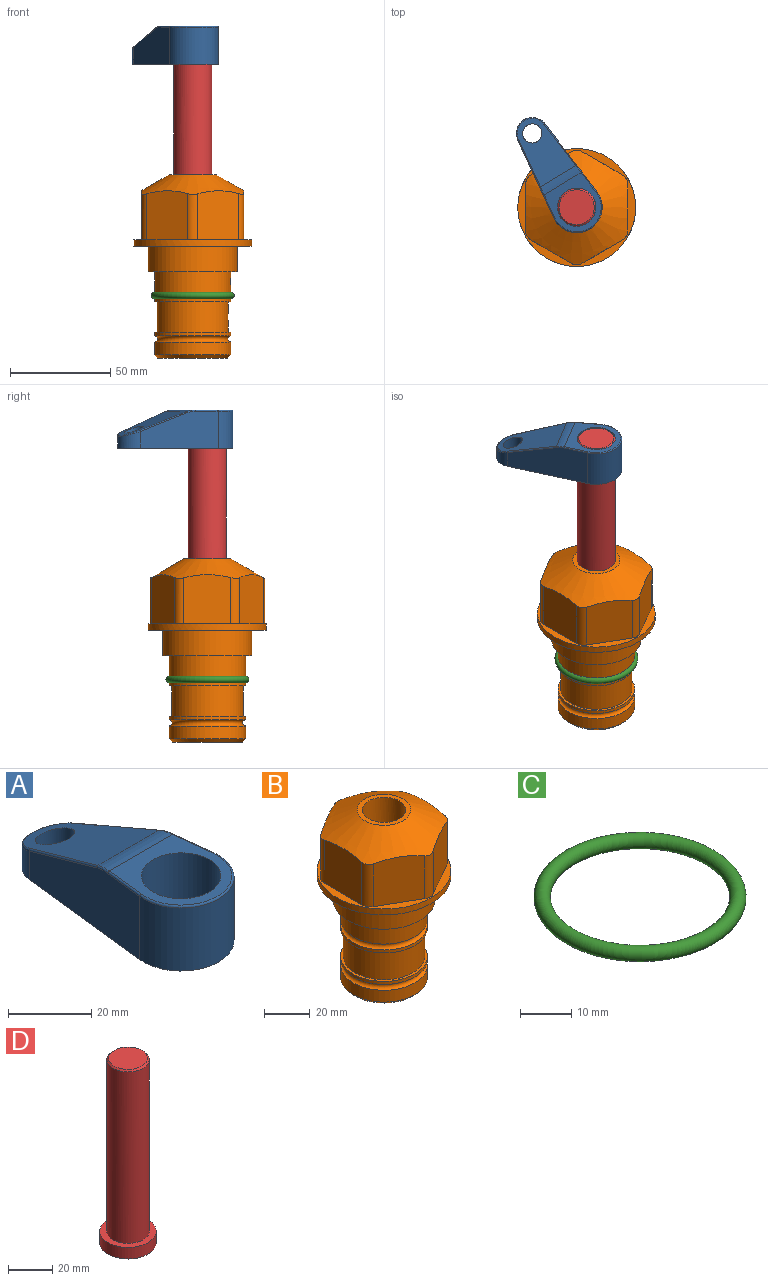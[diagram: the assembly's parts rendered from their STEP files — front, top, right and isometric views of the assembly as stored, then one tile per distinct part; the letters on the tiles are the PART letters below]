
ASSEMBLY  parts=4 mates=2
PART A: 44 faces, bbox 27.5x64.5x19.1 mm
  f0: plane 2.3x0.95mm, normal (0,0,-1), area 1mm2, adj f25,f30,f34
  f1: plane 63.5x25.4mm, normal (0,0,-1), area 561.7mm2, adj f2,f3,f4,f5,f6,f7,f19,f20
  f2: cylinder r=12.7mm len=25.4mm, axis (0,0,-1), area 792.2mm2, adj f1,f3,f5,f13
  f3: plane 42.33x18.54mm, normal (0.99,0.11,0), area 647mm2, adj f1,f2,f4,f11,f12,f14
  f4: cylinder r=7.94mm len=15.78mm, axis (0,0,-1), area 158.6mm2, adj f1,f3,f5,f16
  f5: plane 42.33x18.54mm, normal (-0.99,0.11,0), area 647mm2, adj f1,f2,f4,f15,f17,f18
  f6: cylinder r=9.53mm len=19.05mm, axis (0,0,-1), area 1140.1mm2, adj f1,f8
  f7: cylinder r=4.76mm len=10.98mm, axis (0,0,-1), area 276.1mm2, adj f1,f9
  f8: plane 25.83x24.38mm, normal (0,0,1), area 262.2mm2, adj f6,f10,f11,f13,f15
  f9: plane 32.49x20.55mm, normal (0,0.34,0.94), area 489.9mm2, adj f7,f10,f14,f16,f18
  f10: cylinder r=12.7mm len=21.49mm, axis (-1,0,0), area 93.2mm2, adj f8,f9,f12,f17
  f11: cylinder r=0.51mm len=12.34mm, axis (0.11,-0.99,0), area 9.9mm2, adj f3,f8,f12,f13
  f12: bspline ~7.62x1.64mm, area 3.5mm2, adj f3,f10,f11,f14
  f13: torus R=12.19mm, axis (0,0,1), area 33.6mm2, adj f2,f8,f11,f15
  f14: cylinder r=0.51mm len=26.01mm, axis (0.1,-0.93,0.34), area 21.6mm2, adj f3,f9,f12,f16
  f15: cylinder r=0.51mm len=12.34mm, axis (0.11,0.99,0), area 9.9mm2, adj f5,f8,f13,f17
  f16: bspline ~15.78x7.05mm, area 15.7mm2, adj f4,f9,f14,f18
  f17: bspline ~7.62x1.64mm, area 3.5mm2, adj f5,f10,f15,f18
  f18: cylinder r=0.51mm len=26.01mm, axis (0.1,0.93,-0.34), area 21.6mm2, adj f5,f9,f16,f17
  f19: plane 21.6x14.29mm, normal (-0.99,-0.11,0), area 242.6mm2, adj f1,f26,f28,f34,f36,f38
  f20: plane 21.6x14.29mm, normal (0.99,-0.11,0), area 242.6mm2, adj f1,f27,f29,f37,f39,f41
  f21: cylinder r=12.7mm len=14.29mm, axis (0,0,-1), area 173.2mm2, adj f1,f26,f27,f30,f31,f33
  f22: cylinder r=7.94mm len=7.63mm, axis (0,0,-1), area 53.8mm2, adj f1,f28,f29,f42
  f23: plane 2.3x0.95mm, normal (0,0,-1), area 1mm2, adj f25,f33,f37
  f24: plane 17.94x12.32mm, normal (0,-0.34,-0.94), area 191.2mm2, adj f25,f38,f41,f42
  f25: cylinder r=9.53mm len=12.93mm, axis (-1,0,0), area 37.5mm2, adj f0,f23,f24,f31,f36,f39
  f26: cylinder r=1.59mm len=14.29mm, axis (0,0,-1), area 49mm2, adj f1,f19,f21,f32
  f27: cylinder r=1.59mm len=14.29mm, axis (0,0,-1), area 49mm2, adj f1,f20,f21,f35
  f28: cylinder r=1.59mm len=7.28mm, axis (0,0,-1), area 22.1mm2, adj f1,f19,f22,f40
  f29: cylinder r=1.59mm len=7.28mm, axis (0,0,-1), area 22.1mm2, adj f1,f20,f22,f43
  f30: torus R=14.29mm, axis (0,0,1), area 5.8mm2, adj f0,f21,f31,f32
  f31: bspline ~11.06x2.73mm, area 20.8mm2, adj f21,f25,f30,f33
  f32: sphere r=1.59mm, area 5.4mm2, adj f26,f30,f34
  f33: torus R=14.29mm, axis (0,0,1), area 5.8mm2, adj f21,f23,f31,f35
  f34: cylinder r=1.59mm len=1.68mm, axis (-0.11,0.99,0), area 2.4mm2, adj f0,f19,f32,f36
  f35: sphere r=1.59mm, area 5.4mm2, adj f27,f33,f37
  f36: bspline ~5.82x2.33mm, area 7.7mm2, adj f19,f25,f34,f38
  f37: cylinder r=1.59mm len=1.68mm, axis (0.11,0.99,0), area 2.4mm2, adj f20,f23,f35,f39
  f38: cylinder r=1.59mm len=18.33mm, axis (0.1,-0.93,0.34), area 46.7mm2, adj f19,f24,f36,f40
  f39: bspline ~5.82x2.33mm, area 7.7mm2, adj f20,f25,f37,f41
  f40: sphere r=1.59mm, area 3.6mm2, adj f28,f38,f42
  f41: cylinder r=1.59mm len=18.33mm, axis (0.1,0.93,-0.34), area 46.7mm2, adj f20,f24,f39,f43
  f42: bspline ~8.31x1.84mm, area 15.3mm2, adj f22,f24,f40,f43
  f43: sphere r=1.59mm, area 3.6mm2, adj f29,f41,f42
PART B: 36 faces, bbox 58.7x58.7x91.2 mm
  f0: cylinder r=17.78mm len=35.56mm, axis (0,0,1), area 1670.8mm2, adj f23,f24,f31
  f1: cylinder r=19.05mm len=38.1mm, axis (0,0,1), area 1191.9mm2, adj f26,f27,f30
  f2: plane 58.66x58.66mm, normal (0,0,-1), area 1150.6mm2, adj f3,f28
  f3: cylinder r=29.33mm len=58.66mm, axis (0,0,-1), area 585.1mm2, adj f2,f4
  f4: plane 58.66x58.66mm, normal (0,0,1), area 475.9mm2, adj f3,f5,f6,f7,f8,f9,f10,f11
  f5: plane 24.5x20.32mm, normal (-0.5,0.87,0), area 562.8mm2, adj f4,f15,f16,f17
  f6: plane 24.5x20.32mm, normal (0.5,0.87,0), area 562.8mm2, adj f4,f14,f15,f17
  f7: plane 24.5x23.48mm, normal (1,0,0), area 562.8mm2, adj f4,f13,f14,f17
  f8: plane 24.5x20.32mm, normal (0.5,-0.87,0), area 562.8mm2, adj f4,f12,f13,f17
  f9: plane 24.5x20.32mm, normal (-0.5,-0.87,0), area 562.8mm2, adj f4,f11,f12,f17
  f10: plane 24.5x23.48mm, normal (-1,0,0), area 562.8mm2, adj f4,f11,f16,f17
  f11: cylinder r=5.08mm len=23.01mm, axis (0,0,-1), area 121.2mm2, adj f4,f9,f10,f17
  f12: cylinder r=5.08mm len=23.01mm, axis (0,0,-1), area 121.2mm2, adj f4,f8,f9,f17
  f13: cylinder r=5.08mm len=23.01mm, axis (0,0,-1), area 121.2mm2, adj f4,f7,f8,f17
  f14: cylinder r=5.08mm len=23.01mm, axis (0,0,-1), area 121.2mm2, adj f4,f6,f7,f17
  f15: cylinder r=5.08mm len=23.01mm, axis (0,0,-1), area 121.2mm2, adj f4,f5,f6,f17
  f16: cylinder r=5.08mm len=23.01mm, axis (0,0,-1), area 121.2mm2, adj f4,f5,f10,f17
  f17: cone r=11.73mm half-angle=60deg, axis (0,0,-1), area 2071.8mm2, adj f5,f6,f7,f8,f9,f10,f11,f12
  f18: plane 23.46x23.46mm, normal (0,0,1), area 147.4mm2, adj f17,f35
  f19: plane 34.93x34.93mm, normal (0,0,-1), area 958mm2, adj f29
  f20: cylinder r=19.05mm len=38.1mm, axis (0,0,1), area 760.1mm2, adj f21,f29
  f21: torus R=19.05mm, axis (0,0,1), area 565.3mm2, adj f20,f22
  f22: cylinder r=19.05mm len=38.1mm, axis (0,0,1), area 190mm2, adj f21,f23
  f23: plane 38.1x38.1mm, normal (0,0,1), area 146.9mm2, adj f0,f22
  f24: plane 38.1x38.1mm, normal (0,0,-1), area 146.9mm2, adj f0,f25
  f25: cylinder r=19.05mm len=38.1mm, axis (0,0,1), area 190mm2, adj f24,f26
  f26: torus R=19.05mm, axis (0,0,1), area 565.3mm2, adj f1,f25
  f27: plane 44.45x44.45mm, normal (0,0,-1), area 411.7mm2, adj f1,f28
  f28: cylinder r=22.23mm len=44.45mm, axis (0,0,1), area 1773.5mm2, adj f2,f27
  f29: cone r=19.05mm half-angle=45deg, axis (0,0,1), area 257.5mm2, adj f19,f20
  f30: cylinder r=3.17mm len=6.75mm, axis (-1,0,0), area 128mm2, adj f1,f33
  f31: cylinder r=3.17mm len=6.35mm, axis (-1,0,0), area 102.5mm2, adj f0,f33
  f32: plane 25.4x25.4mm, normal (0,0,1), area 506.7mm2, adj f33
  f33: cylinder r=12.7mm len=66.42mm, axis (0,0,-1), area 5236.2mm2, adj f30,f31,f32,f34
  f34: cone r=9.53mm half-angle=30deg, axis (0,0,-1), area 443.4mm2, adj f33,f35
  f35: cylinder r=9.53mm len=19.05mm, axis (0,0,-1), area 849mm2, adj f18,f34
PART C: 1 faces, bbox 44.7x44.7x3.2 mm
  f0: torus R=19.05mm, axis (0,0,1), area 1193.9mm2
PART D: 6 faces, bbox 25.4x25.4x101.6 mm
  f0: plane 17.46x17.46mm, normal (0,0,1), area 239.5mm2, adj f5
  f1: plane 25.4x25.4mm, normal (0,0,-1), area 506.7mm2, adj f2
  f2: cylinder r=12.7mm len=25.4mm, axis (0,0,1), area 506.7mm2, adj f1,f3
  f3: plane 25.4x25.4mm, normal (0,0,1), area 221.7mm2, adj f2,f4
  f4: cylinder r=9.53mm len=94.46mm, axis (0,0,1), area 5653mm2, adj f3,f5
  f5: cone r=8.73mm half-angle=45deg, axis (0,0,-1), area 64.4mm2, adj f0,f4
PLACE A rot(axis=(0,0,1),31.1deg) t=(0,0,90.61)mm
PLACE B at identity fixed
PLACE C at identity
PLACE D rot(axis=(0,0,1),31.1deg) t=(0,0,36)mm
MATE cylindrical D.f2 <-> B.f0  axis (0,0,1) through (0,0,61.64)mm
MATE fastened A.f2 <-> D.f2  axis (0,0,-1) through (0,0,109.66)mm
